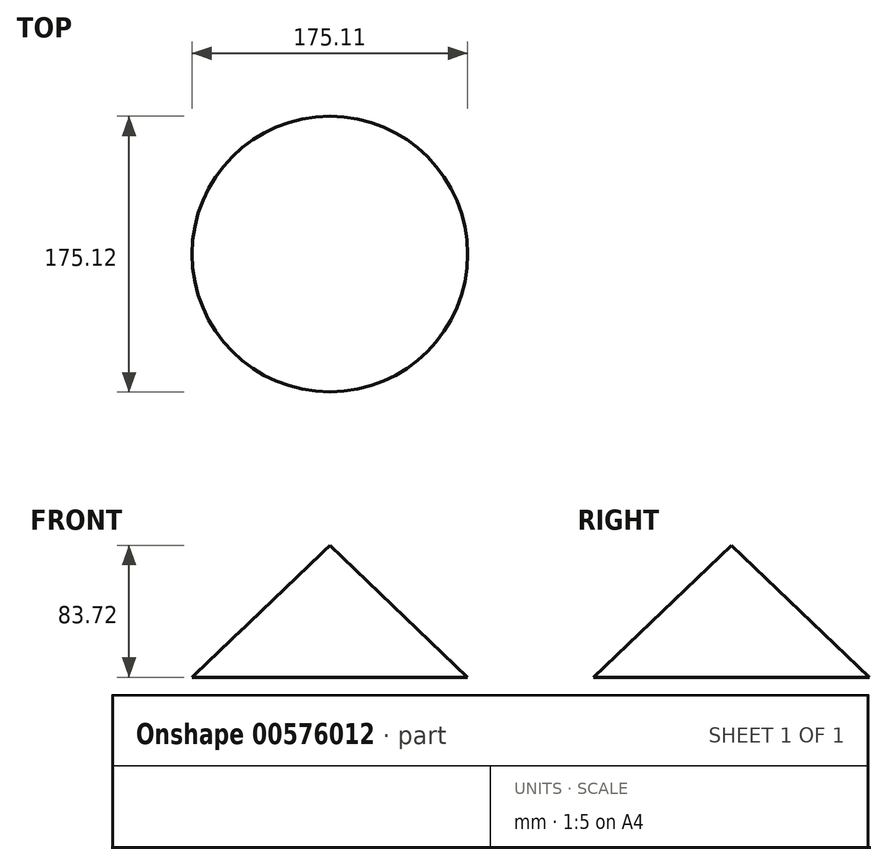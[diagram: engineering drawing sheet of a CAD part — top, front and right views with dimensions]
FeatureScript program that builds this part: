
annotation { "Feature Type Name" : "Feature", "Feature Type Description" : "" }
export const myFeature = defineFeature(function(context is Context, id is Id, definition is map)
    precondition{}
    {
        {
            var Q0;
            Q0=qCreatedBy(makeId("Front.planeOp"),FACE);
            var sketch = newSketch(context, id + "F0", { "sketchPlane" : qUnion([Q0])});
            skLineSegment(sketch, "E0", {"start": v(-32.11, 28.4) * mm, "end": v(-32.11, -55.3) * mm});
            skLineSegment(sketch, "E1", {"start": v(-32.11, -55.3) * mm, "end": v(55.44, -55.3) * mm});
            skLineSegment(sketch, "E2", {"start": v(55.44, -55.3) * mm, "end": v(-32.11, 28.4) * mm});
            skSolve(sketch);
        }
        {
            var Q0;
            Q0=makeQuery(id+"F0.imprint","IMPRINT",FACE,{"disambiguationData":[TD([[makeQuery(id+"F0.imprint","IMPRINT",EDGE,{"derivedFrom":sQuery(id+"F0.wireOp",EDGE,"E0")}),1.0]])]});
            var Q1;
            Q1=sQuery(id+"F0.wireOp",EDGE,"E0");
            revolve(context, id + "F1", {"entities" : qUnion([Q0]), "axis" : qUnion([Q1]), "revolveType" : RevolveType.FULL});
        }
    });
